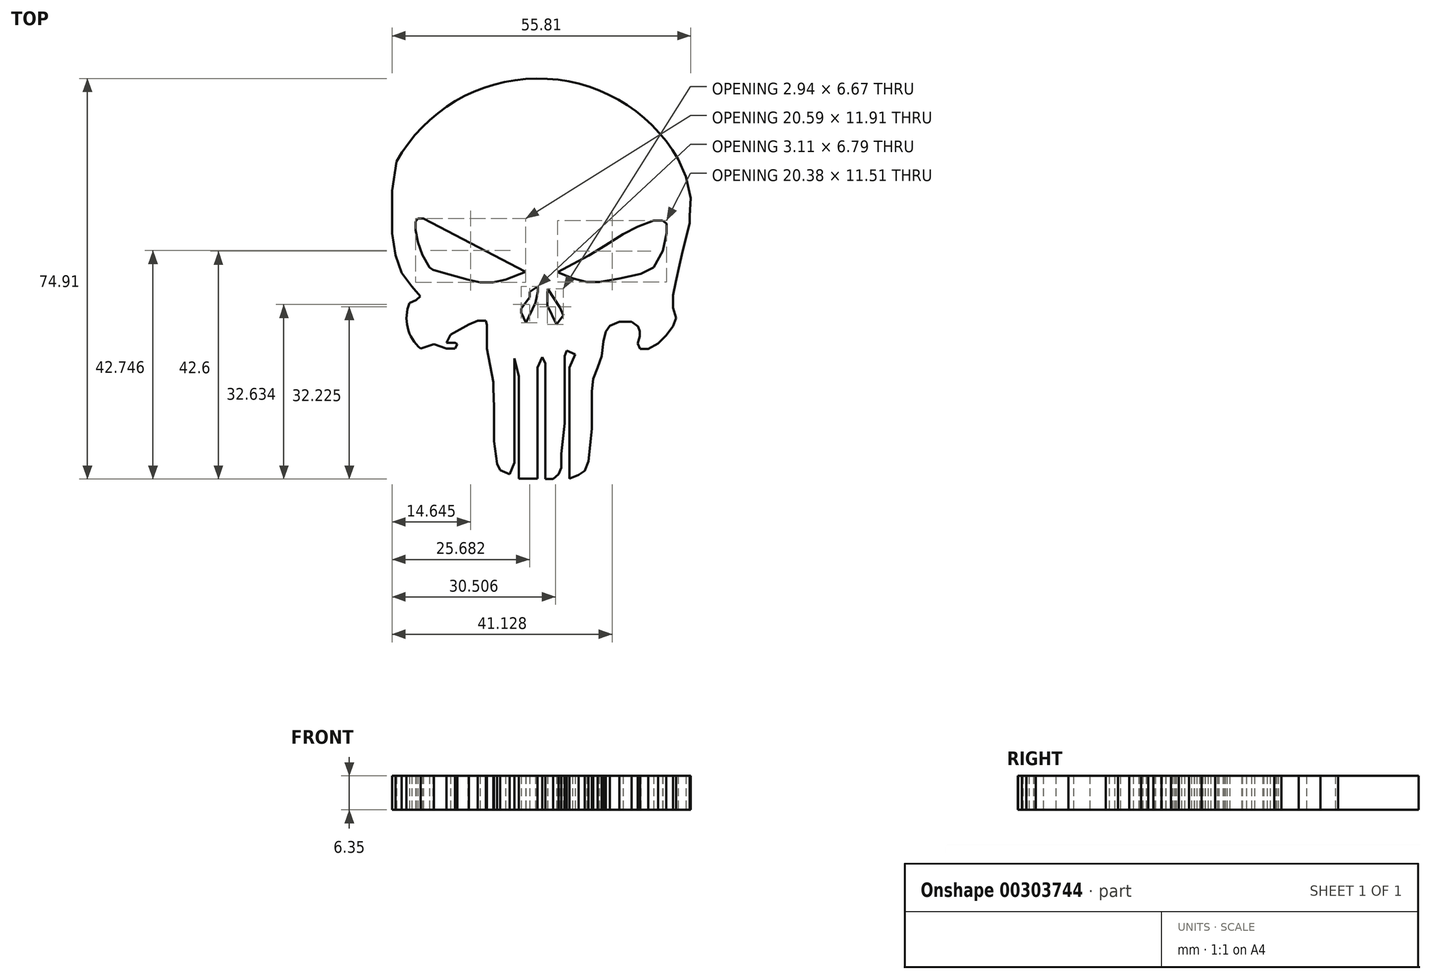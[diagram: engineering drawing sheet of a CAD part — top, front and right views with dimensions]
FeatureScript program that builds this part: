
annotation { "Feature Type Name" : "Feature", "Feature Type Description" : "" }
export const myFeature = defineFeature(function(context is Context, id is Id, definition is map)
    precondition{}
    {
        {
            var Q0;
            Q0=qCreatedBy(makeId("Top.planeOp"),FACE);
            var sketch = newSketch(context, id + "F0", { "sketchPlane" : qUnion([Q0])});
            skLineSegment(sketch, "E0", {"start": v(-29.25, 23.35) * mm, "end": v(-30.07, 17.92) * mm});
            skLineSegment(sketch, "E1", {"start": v(-30.07, 17.92) * mm, "end": v(-30.07, 15.16) * mm});
            skLineSegment(sketch, "E2", {"start": v(-30.07, 15.16) * mm, "end": v(-30.07, 12.4) * mm});
            skLineSegment(sketch, "E3", {"start": v(-30.07, 12.4) * mm, "end": v(-30.07, 9.9) * mm});
            skLineSegment(sketch, "E4", {"start": v(-30.07, 9.9) * mm, "end": v(-29.42, 5.84) * mm});
            skLineSegment(sketch, "E5", {"start": v(-29.42, 5.84) * mm, "end": v(-28.28, 2.52) * mm});
            skLineSegment(sketch, "E6", {"start": v(-28.28, 2.52) * mm, "end": v(-26.42, 0) * mm});
            skLineSegment(sketch, "E7", {"start": v(-26.42, 0) * mm, "end": v(-24.8, -1.86) * mm});
            skLineSegment(sketch, "E8", {"start": v(-24.8, -1.86) * mm, "end": v(-25.59, -2.55) * mm});
            skLineSegment(sketch, "E9", {"start": v(-25.59, -2.55) * mm, "end": v(-26.8, -3.1) * mm});
            skArc(sketch, "E10", {"start": v(-26.8, -3.1) * mm, "mid": v(-27.19, -7.7) * mm, "end": v(-24.74, -11.63) * mm});
            skLineSegment(sketch, "E11", {"start": v(-24.74, -11.63) * mm, "end": v(-22.26, -10.77) * mm});
            skLineSegment(sketch, "E12", {"start": v(-22.26, -10.77) * mm, "end": v(-19.92, -11.63) * mm});
            skLineSegment(sketch, "E13", {"start": v(-19.92, -11.63) * mm, "end": v(-18.36, -11.63) * mm});
            skLineSegment(sketch, "E14", {"start": v(-18.36, -11.63) * mm, "end": v(-17.88, -10.8) * mm});
            skLineSegment(sketch, "E15", {"start": v(-17.88, -10.8) * mm, "end": v(-18.36, -10.53) * mm});
            skLineSegment(sketch, "E16", {"start": v(-18.36, -10.53) * mm, "end": v(-19.92, -10.53) * mm});
            skLineSegment(sketch, "E17", {"start": v(-19.92, -10.53) * mm, "end": v(-19.14, -9.05) * mm});
            skLineSegment(sketch, "E18", {"start": v(-19.14, -9.05) * mm, "end": v(-15.7, -7.1) * mm});
            skLineSegment(sketch, "E19", {"start": v(-15.7, -7.1) * mm, "end": v(-14.06, -6.39) * mm});
            skLineSegment(sketch, "E20", {"start": v(-14.06, -6.39) * mm, "end": v(-12.57, -6.39) * mm});
            skLineSegment(sketch, "E21", {"start": v(-12.57, -6.39) * mm, "end": v(-12.34, -7.27) * mm});
            skLineSegment(sketch, "E22", {"start": v(-12.34, -7.27) * mm, "end": v(-12.34, -11.63) * mm});
            skLineSegment(sketch, "E23", {"start": v(-12.34, -11.63) * mm, "end": v(-11.16, -17.94) * mm});
            skLineSegment(sketch, "E24", {"start": v(-11.16, -16.87) * mm, "end": v(-11.16, -17.94) * mm});
            skLineSegment(sketch, "E25", {"start": v(-11.16, -16.87) * mm, "end": v(-11.16, -17.8) * mm});
            skLineSegment(sketch, "E26", {"start": v(-11.16, -17.8) * mm, "end": v(-11.16, -18.98) * mm});
            skLineSegment(sketch, "E27", {"start": v(-11.16, -18.98) * mm, "end": v(-11, -22.58) * mm});
            skLineSegment(sketch, "E28", {"start": v(-11, -22.58) * mm, "end": v(-11, -24.7) * mm});
            skLineSegment(sketch, "E29", {"start": v(-11, -24.7) * mm, "end": v(-11, -28.95) * mm});
            skLineSegment(sketch, "E30", {"start": v(-11, -28.95) * mm, "end": v(-10.45, -33.13) * mm});
            skLineSegment(sketch, "E31", {"start": v(-10.45, -33.13) * mm, "end": v(-9.88, -34.33) * mm});
            skLineSegment(sketch, "E32", {"start": v(-9.88, -34.33) * mm, "end": v(-8.1, -35.1) * mm});
            skLineSegment(sketch, "E33", {"start": v(-8.1, -35.1) * mm, "end": v(-7.2, -32.98) * mm});
            skLineSegment(sketch, "E34", {"start": v(-7.2, -32.98) * mm, "end": v(-7.2, -30.36) * mm});
            skLineSegment(sketch, "E35", {"start": v(-7.2, -30.36) * mm, "end": v(-7.2, -26.68) * mm});
            skLineSegment(sketch, "E36", {"start": v(-7.2, -26.68) * mm, "end": v(-7.2, -23) * mm});
            skLineSegment(sketch, "E37", {"start": v(-7.2, -23) * mm, "end": v(-7.2, -19.39) * mm});
            skLineSegment(sketch, "E38", {"start": v(-7.2, -19.39) * mm, "end": v(-7.2, -13.44) * mm});
            skLineSegment(sketch, "E39", {"start": v(-7.2, -13.44) * mm, "end": v(-6.41, -16.84) * mm});
            skLineSegment(sketch, "E40", {"start": v(-6.41, -16.84) * mm, "end": v(-6.41, -20.52) * mm});
            skLineSegment(sketch, "E41", {"start": v(-6.41, -20.52) * mm, "end": v(-6.41, -24.56) * mm});
            skLineSegment(sketch, "E42", {"start": v(-6.41, -24.56) * mm, "end": v(-6.41, -28.8) * mm});
            skLineSegment(sketch, "E43", {"start": v(-6.41, -28.8) * mm, "end": v(-6.41, -34.54) * mm});
            skLineSegment(sketch, "E44", {"start": v(-6.41, -34.54) * mm, "end": v(-6.41, -35.96) * mm});
            skLineSegment(sketch, "E45", {"start": v(-6.41, -35.96) * mm, "end": v(-2.87, -35.96) * mm});
            skLineSegment(sketch, "E46", {"start": v(-2.87, -35.96) * mm, "end": v(-2.87, -15.21) * mm});
            skLineSegment(sketch, "E47", {"start": v(-2.87, -15.21) * mm, "end": v(-2.02, -13.23) * mm});
            skLineSegment(sketch, "E48", {"start": v(-2.02, -13.23) * mm, "end": v(-1.46, -14.43) * mm});
            skLineSegment(sketch, "E49", {"start": v(-1.46, -14.43) * mm, "end": v(-1.46, -16.48) * mm});
            skLineSegment(sketch, "E50", {"start": v(-1.46, -16.48) * mm, "end": v(-1.46, -21.16) * mm});
            skLineSegment(sketch, "E51", {"start": v(-1.46, -21.16) * mm, "end": v(-1.46, -36.03) * mm});
            skLineSegment(sketch, "E52", {"start": v(-1.46, -36.03) * mm, "end": v(0, -36.03) * mm});
            skLineSegment(sketch, "E53", {"start": v(0, -36.03) * mm, "end": v(1.02, -35.1) * mm});
            skLineSegment(sketch, "E54", {"start": v(1.02, -35.1) * mm, "end": v(1.53, -33.92) * mm});
            skLineSegment(sketch, "E55", {"start": v(1.53, -33.92) * mm, "end": v(1.53, -31.29) * mm});
            skLineSegment(sketch, "E56", {"start": v(1.53, -31.29) * mm, "end": v(2.16, -25.62) * mm});
            skLineSegment(sketch, "E57", {"start": v(2.16, -25.62) * mm, "end": v(2.16, -20.66) * mm});
            skLineSegment(sketch, "E58", {"start": v(2.16, -20.66) * mm, "end": v(2.16, -16.48) * mm});
            skLineSegment(sketch, "E59", {"start": v(2.16, -16.48) * mm, "end": v(2.16, -13.01) * mm});
            skLineSegment(sketch, "E60", {"start": v(2.16, -13.01) * mm, "end": v(2.59, -12) * mm});
            skLineSegment(sketch, "E61", {"start": v(2.59, -12) * mm, "end": v(4.16, -12.68) * mm});
            skLineSegment(sketch, "E62", {"start": v(4.16, -12.68) * mm, "end": v(3.75, -13.63) * mm});
            skLineSegment(sketch, "E63", {"start": v(3.75, -13.63) * mm, "end": v(3.08, -15.21) * mm});
            skLineSegment(sketch, "E64", {"start": v(3.08, -15.21) * mm, "end": v(3.08, -17.26) * mm});
            skLineSegment(sketch, "E65", {"start": v(3.08, -17.26) * mm, "end": v(3.08, -35.96) * mm});
            skLineSegment(sketch, "E66", {"start": v(3.08, -35.96) * mm, "end": v(4.78, -35.25) * mm});
            skLineSegment(sketch, "E67", {"start": v(4.78, -35.25) * mm, "end": v(5.9, -34.47) * mm});
            skLineSegment(sketch, "E68", {"start": v(5.9, -34.47) * mm, "end": v(6.62, -32.7) * mm});
            skLineSegment(sketch, "E69", {"start": v(6.62, -32.7) * mm, "end": v(6.87, -30.4) * mm});
            skLineSegment(sketch, "E70", {"start": v(6.87, -30.4) * mm, "end": v(7.1, -28.28) * mm});
            skLineSegment(sketch, "E71", {"start": v(7.1, -28.28) * mm, "end": v(7.3, -26.58) * mm});
            skLineSegment(sketch, "E72", {"start": v(7.3, -26.58) * mm, "end": v(7.3, -24.2) * mm});
            skLineSegment(sketch, "E73", {"start": v(7.3, -24.2) * mm, "end": v(7.3, -21.87) * mm});
            skLineSegment(sketch, "E74", {"start": v(7.3, -21.87) * mm, "end": v(7.3, -19.6) * mm});
            skLineSegment(sketch, "E75", {"start": v(7.3, -19.6) * mm, "end": v(7.46, -18.08) * mm});
            skLineSegment(sketch, "E76", {"start": v(7.46, -18.08) * mm, "end": v(7.54, -17.29) * mm});
            skLineSegment(sketch, "E77", {"start": v(7.54, -17.29) * mm, "end": v(8.32, -15.21) * mm});
            skLineSegment(sketch, "E78", {"start": v(8.32, -15.21) * mm, "end": v(9.1, -13.01) * mm});
            skLineSegment(sketch, "E79", {"start": v(9.1, -13.01) * mm, "end": v(9.4, -10.3) * mm});
            skLineSegment(sketch, "E80", {"start": v(9.4, -10.3) * mm, "end": v(9.9, -8.42) * mm});
            skLineSegment(sketch, "E81", {"start": v(9.9, -8.42) * mm, "end": v(10.65, -7.34) * mm});
            skLineSegment(sketch, "E82", {"start": v(10.65, -7.34) * mm, "end": v(12.38, -6.59) * mm});
            skLineSegment(sketch, "E83", {"start": v(12.38, -6.59) * mm, "end": v(14.68, -6.59) * mm});
            skLineSegment(sketch, "E84", {"start": v(14.68, -6.59) * mm, "end": v(15.9, -7.48) * mm});
            skLineSegment(sketch, "E85", {"start": v(15.9, -7.48) * mm, "end": v(16.23, -8.37) * mm});
            skLineSegment(sketch, "E86", {"start": v(16.23, -8.37) * mm, "end": v(16.23, -9.36) * mm});
            skLineSegment(sketch, "E87", {"start": v(16.23, -9.36) * mm, "end": v(15.8, -10.67) * mm});
            skLineSegment(sketch, "E88", {"start": v(15.8, -10.67) * mm, "end": v(16.28, -11.66) * mm});
            skLineSegment(sketch, "E89", {"start": v(16.28, -11.66) * mm, "end": v(17.08, -11.66) * mm});
            skLineSegment(sketch, "E90", {"start": v(17.08, -11.66) * mm, "end": v(17.83, -11.66) * mm});
            skLineSegment(sketch, "E91", {"start": v(17.83, -11.66) * mm, "end": v(19.61, -10.67) * mm});
            skLineSegment(sketch, "E92", {"start": v(19.61, -10.67) * mm, "end": v(21.16, -9.17) * mm});
            skLineSegment(sketch, "E93", {"start": v(21.16, -9.17) * mm, "end": v(22.43, -7.43) * mm});
            skLineSegment(sketch, "E94", {"start": v(22.43, -7.43) * mm, "end": v(23.04, -5.93) * mm});
            skLineSegment(sketch, "E95", {"start": v(23.04, -5.93) * mm, "end": v(22.43, -4) * mm});
            skLineSegment(sketch, "E96", {"start": v(22.43, -4) * mm, "end": v(22.43, -1.66) * mm});
            skLineSegment(sketch, "E97", {"start": v(22.43, -1.66) * mm, "end": v(22.94, 0.83) * mm});
            skLineSegment(sketch, "E98", {"start": v(22.94, 0.83) * mm, "end": v(23.65, 3.97) * mm});
            skLineSegment(sketch, "E99", {"start": v(23.65, 3.97) * mm, "end": v(24.12, 6) * mm});
            skLineSegment(sketch, "E100", {"start": v(24.12, 6) * mm, "end": v(25.52, 11.9) * mm});
            skLineSegment(sketch, "E101", {"start": v(25.52, 11.9) * mm, "end": v(25.52, 13.21) * mm});
            skLineSegment(sketch, "E102", {"start": v(25.52, 13.21) * mm, "end": v(25.74, 16.5) * mm});
            skLineSegment(sketch, "E103", {"start": v(25.74, 16.5) * mm, "end": v(24.87, 20.53) * mm});
            skLineSegment(sketch, "E104", {"start": v(24.87, 20.53) * mm, "end": v(23.4, 23.82) * mm});
            skArc(sketch, "E105", {"start": v(23.4, 23.82) * mm, "mid": v(-3.06, 38.87) * mm, "end": v(-29.25, 23.35) * mm});
            skLineSegment(sketch, "E106", {"start": v(0.87, 2.65) * mm, "end": v(3.62, 1.55) * mm});
            skLineSegment(sketch, "E107", {"start": v(3.62, 1.55) * mm, "end": v(6.31, 0.82) * mm});
            skLineSegment(sketch, "E108", {"start": v(6.31, 0.82) * mm, "end": v(8.64, 0.82) * mm});
            skLineSegment(sketch, "E109", {"start": v(8.64, 0.82) * mm, "end": v(12.31, 1.43) * mm});
            skLineSegment(sketch, "E110", {"start": v(12.31, 1.43) * mm, "end": v(16.41, 2.35) * mm});
            skLineSegment(sketch, "E111", {"start": v(16.41, 2.35) * mm, "end": v(18.8, 3.57) * mm});
            skLineSegment(sketch, "E112", {"start": v(18.8, 3.57) * mm, "end": v(20.51, 6.7) * mm});
            skLineSegment(sketch, "E113", {"start": v(20.51, 6.7) * mm, "end": v(21.25, 9.94) * mm});
            skLineSegment(sketch, "E114", {"start": v(21.25, 9.94) * mm, "end": v(21.25, 11.77) * mm});
            skLineSegment(sketch, "E115", {"start": v(21.25, 11.77) * mm, "end": v(20.45, 12.32) * mm});
            skLineSegment(sketch, "E116", {"start": v(20.45, 12.32) * mm, "end": v(18.8, 12.32) * mm});
            skLineSegment(sketch, "E117", {"start": v(18.8, 12.32) * mm, "end": v(15.8, 11.16) * mm});
            skLineSegment(sketch, "E118", {"start": v(15.8, 11.16) * mm, "end": v(13.1, 9.75) * mm});
            skLineSegment(sketch, "E119", {"start": v(13.1, 9.75) * mm, "end": v(9.8, 7.67) * mm});
            skLineSegment(sketch, "E120", {"start": v(9.8, 7.67) * mm, "end": v(6.68, 5.77) * mm});
            skLineSegment(sketch, "E121", {"start": v(6.68, 5.77) * mm, "end": v(0.87, 2.65) * mm});
            skLineSegment(sketch, "E122", {"start": v(-0.97, -0.47) * mm, "end": v(1.3, -3.96) * mm});
            skLineSegment(sketch, "E123", {"start": v(1.3, -3.96) * mm, "end": v(1.9, -5.43) * mm});
            skLineSegment(sketch, "E124", {"start": v(1.9, -5.43) * mm, "end": v(0.68, -7.14) * mm});
            skLineSegment(sketch, "E125", {"start": v(0.68, -7.14) * mm, "end": v(-1.04, -3.56) * mm});
            skLineSegment(sketch, "E126", {"start": v(-1.04, -3.56) * mm, "end": v(-1.04, -1.4) * mm});
            skLineSegment(sketch, "E127", {"start": v(-1.04, -1.4) * mm, "end": v(-0.97, -0.47) * mm});
            skLineSegment(sketch, "E128", {"start": v(-5.05, -6.8) * mm, "end": v(-3.25, -3.02) * mm});
            skLineSegment(sketch, "E129", {"start": v(-3.25, -3.02) * mm, "end": v(-2.83, -0.98) * mm});
            skLineSegment(sketch, "E130", {"start": v(-2.83, -0.98) * mm, "end": v(-2.83, 0) * mm});
            skLineSegment(sketch, "E131", {"start": v(-2.83, 0) * mm, "end": v(-4.39, -1.04) * mm});
            skLineSegment(sketch, "E132", {"start": v(-4.39, -1.04) * mm, "end": v(-4.39, -2.06) * mm});
            skLineSegment(sketch, "E133", {"start": v(-4.39, -2.06) * mm, "end": v(-5.94, -4.16) * mm});
            skLineSegment(sketch, "E134", {"start": v(-5.94, -4.16) * mm, "end": v(-5.94, -4.88) * mm});
            skLineSegment(sketch, "E135", {"start": v(-5.94, -4.88) * mm, "end": v(-5.05, -6.8) * mm});
            skLineSegment(sketch, "E136", {"start": v(-5.13, 2.73) * mm, "end": v(-24.22, 12.67) * mm});
            skLineSegment(sketch, "E137", {"start": v(-24.22, 12.67) * mm, "end": v(-25.26, 12.67) * mm});
            skLineSegment(sketch, "E138", {"start": v(-25.26, 12.67) * mm, "end": v(-25.72, 12.1) * mm});
            skLineSegment(sketch, "E139", {"start": v(-25.72, 12.1) * mm, "end": v(-25.72, 10.56) * mm});
            skLineSegment(sketch, "E140", {"start": v(-25.72, 10.56) * mm, "end": v(-25.26, 8.24) * mm});
            skLineSegment(sketch, "E141", {"start": v(-25.26, 8.24) * mm, "end": v(-24.45, 5.93) * mm});
            skLineSegment(sketch, "E142", {"start": v(-24.45, 5.93) * mm, "end": v(-23.08, 3.57) * mm});
            skLineSegment(sketch, "E143", {"start": v(-23.08, 3.57) * mm, "end": v(-22.49, 3.08) * mm});
            skLineSegment(sketch, "E144", {"start": v(-22.49, 3.08) * mm, "end": v(-20.48, 2.52) * mm});
            skLineSegment(sketch, "E145", {"start": v(-20.48, 2.52) * mm, "end": v(-15.92, 1.25) * mm});
            skLineSegment(sketch, "E146", {"start": v(-15.92, 1.25) * mm, "end": v(-13.63, 0.76) * mm});
            skLineSegment(sketch, "E147", {"start": v(-13.63, 0.76) * mm, "end": v(-11.24, 0.76) * mm});
            skLineSegment(sketch, "E148", {"start": v(-11.24, 0.76) * mm, "end": v(-8.86, 1.25) * mm});
            skLineSegment(sketch, "E149", {"start": v(-8.86, 1.25) * mm, "end": v(-5.13, 2.73) * mm});
            skSolve(sketch);
        }
        {
            var Q0;
            Q0=makeQuery(id+"F0.imprint","IMPRINT",FACE,{"disambiguationData":[TD([[makeQuery(id+"F0.imprint","IMPRINT",EDGE,{"derivedFrom":sQuery(id+"F0.wireOp",EDGE,"E0")}),1.0]])]});
            extrude(context, id + "F1", {"entities" : qUnion([Q0]), "depth" : 6.35 * mm});
        }
    });
